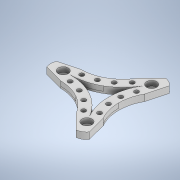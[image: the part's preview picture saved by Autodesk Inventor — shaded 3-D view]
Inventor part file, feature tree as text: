
AUTODESK INVENTOR PART (.ipt)
format: ipt  version: 2022.4 (Build 264492010, 492A)  size: 217,088 bytes
history: native  units: mm
features: other x3, extrude x1, sketch x1
ambient origin geometry x8: Origin, YZ Plane, XZ Plane, XY Plane, X Axis, Y Axis, Z Axis, Center Point
bodies: Solid1 (feature_tree)
feature tree (5):
  other  "Fidget_bottom_3cm.ipt"
  extrude  "Extrusion1"  Depth=10.0mm TaperAngle=360.0deg
  other  "Solid4::Fidget_bottom_3cm.ipt"
  other  "TaggingFeature1"
  sketch  "Sketch1"  dims[d0=10.0mm d1=30.0mm d3=360.0deg d5=10.0mm d6=0.0mm]
